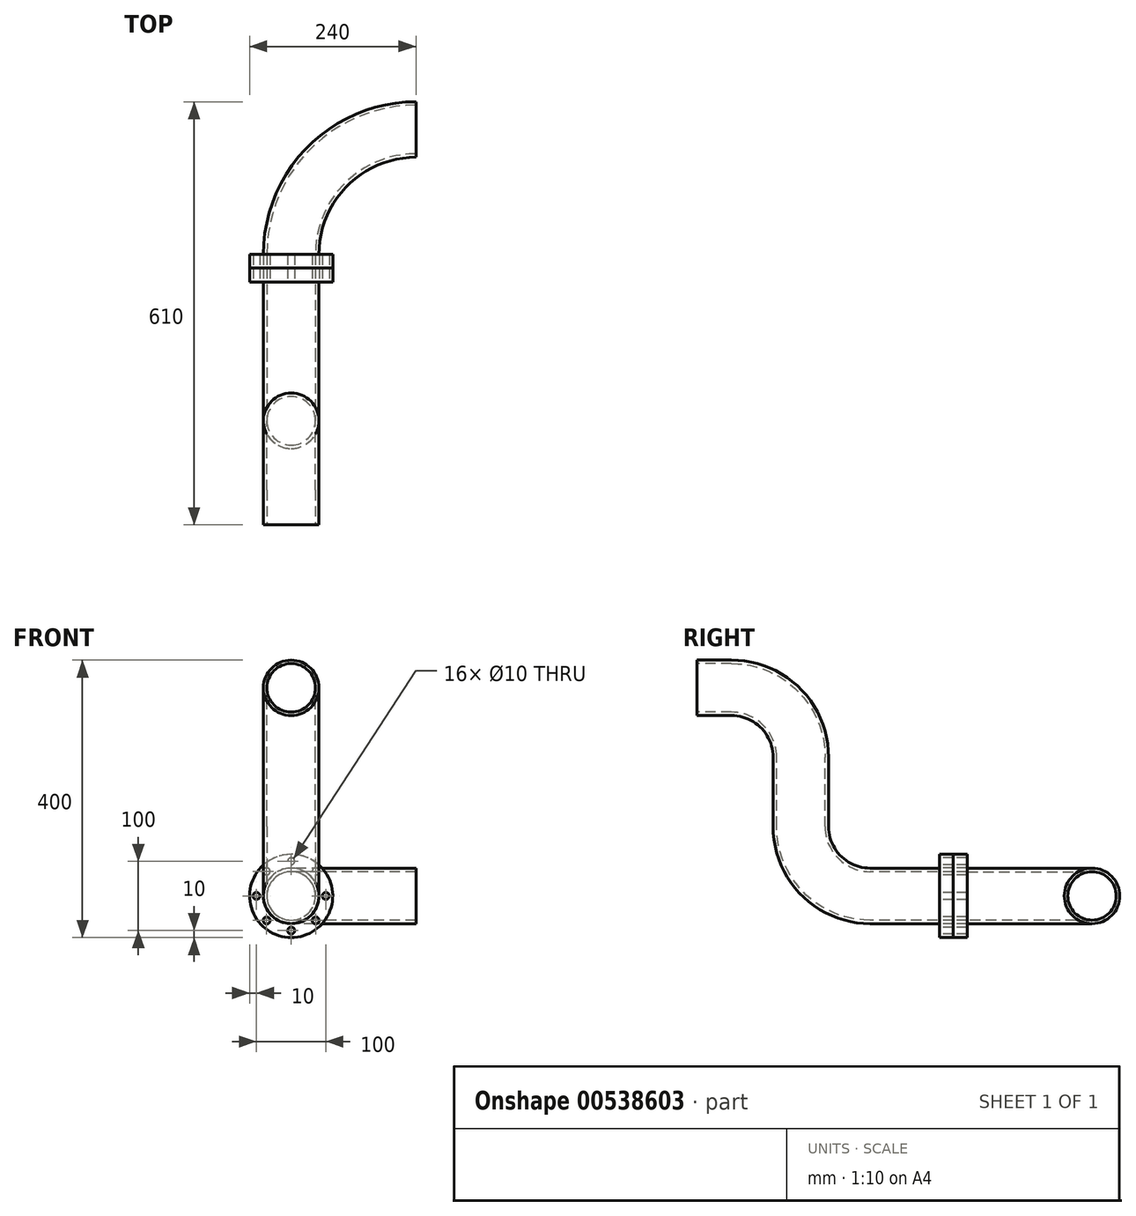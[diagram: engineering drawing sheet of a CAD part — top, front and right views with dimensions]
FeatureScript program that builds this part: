
annotation { "Feature Type Name" : "Feature", "Feature Type Description" : "" }
export const myFeature = defineFeature(function(context is Context, id is Id, definition is map)
    precondition{}
    {
        {
            var Q0;
            Q0=qCreatedBy(makeId("Front.planeOp"),FACE);
            var sketch = newSketch(context, id + "F0", { "sketchPlane" : qUnion([Q0])});
            skCircle(sketch, "E0", {"center": v(0, 0) * mm, "radius": 60 * mm});
            skCircle(sketch, "E1", {"center": v(0, 50) * mm, "radius": 5 * mm});
            skCircle(sketch, "E2.1.0", {"center": v(-35.36, 35.36) * mm, "radius": 5 * mm});
            skCircle(sketch, "E2.2.0", {"center": v(-50, 0) * mm, "radius": 5 * mm});
            skCircle(sketch, "E3.1.3.0", {"center": v(-35.36, -35.36) * mm, "radius": 5 * mm});
            skCircle(sketch, "E3.1.4.0", {"center": v(0, -50) * mm, "radius": 5 * mm});
            skCircle(sketch, "E3.1.5.0", {"center": v(35.36, -35.36) * mm, "radius": 5 * mm});
            skCircle(sketch, "E3.1.6.0", {"center": v(50, 0) * mm, "radius": 5 * mm});
            skCircle(sketch, "E3.1.7.0", {"center": v(35.36, 35.36) * mm, "radius": 5 * mm});
            skCircle(sketch, "E4", {"center": v(0, 0) * mm, "radius": 35 * mm});
            skSolve(sketch);
        }
        {
            var Q0;
            Q0 = qSketchRegion(id + "F0", true);
            extrude(context, id + "F1", {"entities" : qUnion([Q0]), "oppositeDirection" : true, "depth" : 20 * mm, "offsetDistance" : 25 * mm});
        }
        {
            var Q0;
            Q0=makeQuery(id+"F1.opExtrude","CAP_FACE",FACE,{"disambiguationData":[OSD([sQuery(id+"F0.wireOp",EDGE,"E0"),sQuery(id+"F0.wireOp",EDGE,"E1"),sQuery(id+"F0.wireOp",EDGE,"E2.1.0"),sQuery(id+"F0.wireOp",EDGE,"E2.2.0"),sQuery(id+"F0.wireOp",EDGE,"E3.1.3.0"),sQuery(id+"F0.wireOp",EDGE,"E3.1.4.0"),sQuery(id+"F0.wireOp",EDGE,"E3.1.5.0"),sQuery(id+"F0.wireOp",EDGE,"E3.1.6.0"),sQuery(id+"F0.wireOp",EDGE,"E3.1.7.0"),sQuery(id+"F0.wireOp",EDGE,"E4")])],"isStart":false});
            extrude(context, id + "F2", {"entities" : qUnion([Q0]), "depth" : 20 * mm, "offsetDistance" : 25 * mm});
        }
        {
            var Q0;
            Q0=qCreatedBy(makeId("Front.planeOp"),FACE);
            var sketch = newSketch(context, id + "F3", { "sketchPlane" : qUnion([Q0])});
            skCircle(sketch, "E5", {"center": v(0, 0) * mm, "radius": 40 * mm});
            skCircle(sketch, "E6", {"center": v(0, 0) * mm, "radius": 35 * mm});
            skSolve(sketch);
        }
        {
            var Q0;
            Q0=qCreatedBy(makeId("Right.planeOp"),FACE);
            var sketch = newSketch(context, id + "F4", { "sketchPlane" : qUnion([Q0])});
            skLineSegment(sketch, "E7", {"start": v(0, 0) * mm, "end": v(-100, 0) * mm});
            skLineSegment(sketch, "E8", {"start": v(-200, 100) * mm, "end": v(-200, 200) * mm});
            skLineSegment(sketch, "E9", {"start": v(-300, 300) * mm, "end": v(-350, 300) * mm});
            skPoint(sketch, "E10.visualSharp", {"position": v(-200, 0) * mm});
            skArc(sketch, "E10.filletArc", {"start": v(-200, 100) * mm, "mid": v(-170.71, 29.29) * mm, "end": v(-100, 0) * mm});
            skPoint(sketch, "E11.visualSharp", {"position": v(-200, 300) * mm});
            skArc(sketch, "E11.filletArc", {"start": v(-200, 200) * mm, "mid": v(-229.29, 270.71) * mm, "end": v(-300, 300) * mm});
            skSolve(sketch);
        }
        {
            var Q0;
            Q0=makeQuery(id+"F3.imprint","IMPRINT",FACE,{"disambiguationData":[TD([[makeQuery(id+"F3.imprint","IMPRINT",EDGE,{"derivedFrom":sQuery(id+"F3.wireOp",EDGE,"E5")}),1.0]])]});
            var Q1;
            Q1 = qConstructionFilter(qBodyType(qCreatedBy(id + "F4" ,EDGE), BodyType.WIRE), ConstructionObject.NO);
            sweep(context, id + "F5", {"operationType" : NewBodyOperationType.ADD, "profiles" : qUnion([Q0]), "path" : qUnion([Q1])});
        }
        {
            var Q0;
            Q0=makeQuery(id+"F2.opExtrude","CAP_FACE",FACE,{"disambiguationData":[OSD([sQuery(id+"F0.wireOp",EDGE,"E0"),sQuery(id+"F0.wireOp",EDGE,"E1"),sQuery(id+"F0.wireOp",EDGE,"E2.1.0"),sQuery(id+"F0.wireOp",EDGE,"E2.2.0"),sQuery(id+"F0.wireOp",EDGE,"E3.1.3.0"),sQuery(id+"F0.wireOp",EDGE,"E3.1.4.0"),sQuery(id+"F0.wireOp",EDGE,"E3.1.5.0"),sQuery(id+"F0.wireOp",EDGE,"E3.1.6.0"),sQuery(id+"F0.wireOp",EDGE,"E3.1.7.0"),sQuery(id+"F0.wireOp",EDGE,"E4")])],"isStart":false});
            var sketch = newSketch(context, id + "F6", { "sketchPlane" : qUnion([Q0])});
            skCircle(sketch, "E12.0", {"center": v(0, 0) * mm, "radius": 35 * mm});
            skCircle(sketch, "E13", {"center": v(0, 0) * mm, "radius": 40 * mm});
            skLineSegment(sketch, "E14", {"start": v(-180, -128.79) * mm, "end": v(-180, 91.25) * mm, "construction": true});
            skSolve(sketch);
        }
        {
            var Q0;
            Q0 = qSketchRegion(id + "F6", true);
            var Q1;
            Q1=sQuery(id+"F6.wireOp",EDGE,"E14");
            revolve(context, id + "F7", {"operationType" : NewBodyOperationType.ADD, "entities" : qUnion([Q0]), "axis" : qUnion([Q1]), "revolveType" : RevolveType.ONE_DIRECTION, "oppositeDirection" : true, "angle" : 90 * degree});
        }
    });
